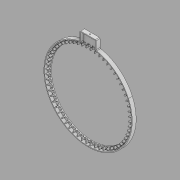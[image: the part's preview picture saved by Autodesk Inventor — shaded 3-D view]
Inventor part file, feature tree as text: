
AUTODESK INVENTOR PART (.ipt)
format: ipt  version: 2020 (Build 240168000, 168)  size: 2,571,776 bytes
history: native  units: mm
features: extrude x7, sketch x5, projected_geometry x4, other x3, fillet x2, split x2, pattern_circular x1, hole x1
ambient origin geometry x8: Origin, YZ Plane, XZ Plane, XY Plane, X Axis, Y Axis, Z Axis, Center Point
bodies: Solid1 (feature_tree), Solid5 (feature_tree)
feature tree (25):
  sketch  "Sketch1"  dims[d0=16.666667mm d7=3.0mm d9=3.0mm d10=0.0mm]
  extrude  "Extrusion1"  Depth=3.0mm TaperAngle=0.0deg
  extrude  "Extrusion2"  Depth=14.2mm
  extrude  "Extrusion3"  Depth=3.0mm
  fillet  "Fillet1"  Radius=3.0mm
  pattern_circular  "Circular Pattern2"  [2 undecoded]
  sketch  "Sketch4"  dims[d13=0.0mm d14=2.8mm d15=3.0mm]
  extrude  "Extrusion9"  Depth=10.0mm
  extrude  "Extrusion10"  Depth=10.0mm
  extrude  "Extrusion11"  Depth=10.0mm
  fillet  "Fillet2"  Radius=600.0mm
  sketch  "Sketch6"  dims[d16=16.2mm d17=0.0mm]
  split  "Split1"
  split  "Split2"
  sketch  "Sketch10"  dims[d32=3.0mm d33=5.0mm d44=29.0mm d45=0.7mm d46=52.0mm d49=1.0mm d50=600.0mm d51=360.0deg d53=10.0mm d54=0.0mm d55=11.2mm d56=0.0mm d57=10.0mm d58=0.0mm d63=0.7mm d70=2.8mm d71=3.0mm d73=235.0mm d91=0.2mm d95=1.75mm d119=3.0mm d129=0.7mm d133=3.0mm d134=6.0mm d135=8.0mm d136=2.0mm d137=90.0deg d138=8.0mm d139=20.594885mm d140=4.0mm d141=10.0mm d142=0.0mm d144=0.7mm d145=0.0mm d77=0.5mm d78=0.872665mm d79=0.5mm d80=0.872665mm]
  hole  "Hole1"  [1 undecoded]
  extrude  "Extrusion18"  Depth=11.2mm TaperAngle=0.0deg
  sketch  "Sketch2"  dims[d11=10.8mm d12=14.2mm]
  projected_geometry  "Projected Loop1"
  projected_geometry  "Projected Loop4"
  projected_geometry  "Projected Loop5"
  projected_geometry  "Projected Loop7"
  other  "Top"
  other  "Right"
  other  "Left"
note: 3 required parameter values undecoded (feature->parameter linkage not recoverable at this tier; creation-order binding heuristic only, values carry confidence <= 0.55)
